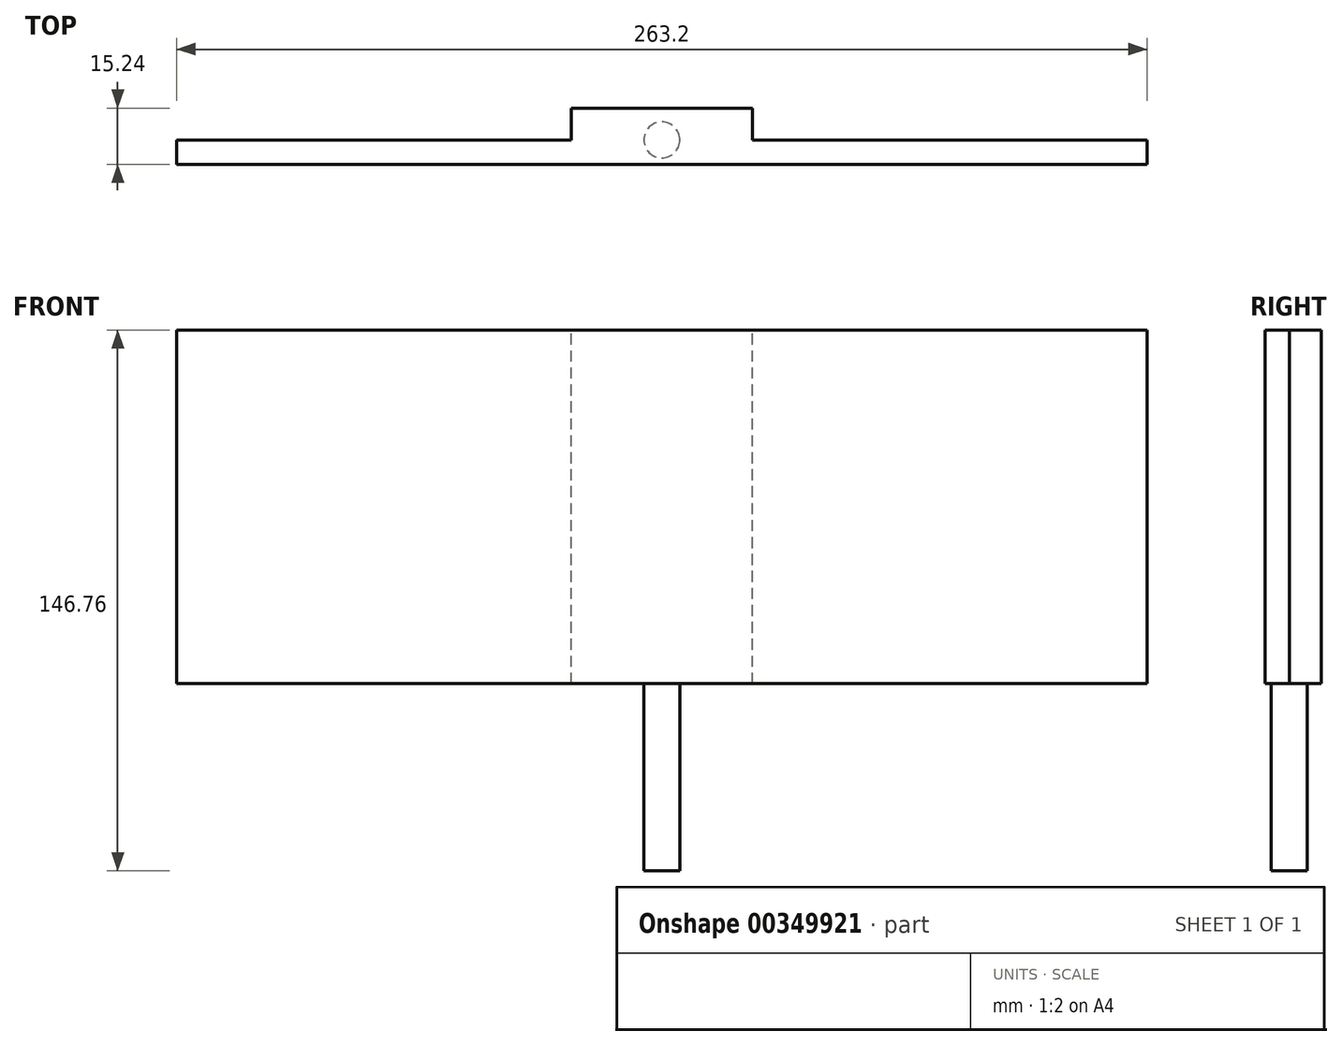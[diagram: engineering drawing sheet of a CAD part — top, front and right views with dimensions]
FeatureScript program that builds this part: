
annotation { "Feature Type Name" : "Feature", "Feature Type Description" : "" }
export const myFeature = defineFeature(function(context is Context, id is Id, definition is map)
    precondition{}
    {
        {
            var Q0;
            Q0=qCreatedBy(makeId("Front.planeOp"),FACE);
            var sketch = newSketch(context, id + "F0", { "sketchPlane" : qUnion([Q0])});
            skLineSegment(sketch, "E0.bottom", {"start": v(131.6, -47.98) * mm, "end": v(-131.6, -47.98) * mm});
            skLineSegment(sketch, "E0.top", {"start": v(131.6, 47.98) * mm, "end": v(-131.6, 47.98) * mm});
            skLineSegment(sketch, "E0.left", {"start": v(131.6, -47.98) * mm, "end": v(131.6, 47.98) * mm});
            skLineSegment(sketch, "E0.right", {"start": v(-131.6, -47.98) * mm, "end": v(-131.6, 47.98) * mm});
            skPoint(sketch, "E0.middle", {"position": v(0, 0) * mm});
            skSolve(sketch);
        }
        {
            var Q0;
            Q0 = qSketchRegion(id + "F0", true);
            extrude(context, id + "F1", {"entities" : qUnion([Q0]), "depth" : 6.6 * mm, "offsetDistance" : 25.4 * mm});
        }
        {
            var Q0;
            Q0=makeQuery(id+"F1.opExtrude","CAP_FACE",FACE,{"disambiguationData":[OSD([sQuery(id+"F0.wireOp",EDGE,"E0.bottom"),sQuery(id+"F0.wireOp",EDGE,"E0.top"),sQuery(id+"F0.wireOp",EDGE,"E0.left"),sQuery(id+"F0.wireOp",EDGE,"E0.right")])],"isStart":true});
            var sketch = newSketch(context, id + "F2", { "sketchPlane" : qUnion([Q0])});
            skLineSegment(sketch, "E1.bottom", {"start": v(24.51, -47.98) * mm, "end": v(-24.51, -47.98) * mm});
            skLineSegment(sketch, "E1.top", {"start": v(24.51, 47.98) * mm, "end": v(-24.51, 47.98) * mm});
            skLineSegment(sketch, "E1.left", {"start": v(24.51, -47.98) * mm, "end": v(24.51, 47.98) * mm});
            skLineSegment(sketch, "E1.right", {"start": v(-24.51, -47.98) * mm, "end": v(-24.51, 47.98) * mm});
            skPoint(sketch, "E1.middle", {"position": v(0, 0) * mm});
            skSolve(sketch);
        }
        {
            var Q0;
            Q0 = qSketchRegion(id + "F2", true);
            extrude(context, id + "F3", {"entities" : qUnion([Q0]), "operationType" : NewBodyOperationType.ADD, "depth" : 8.64 * mm, "offsetDistance" : 25.4 * mm});
        }
        {
            var Q0;
            Q0=makeQuery(id+"F3.boolean.opBoolean","MERGE",FACE,{"derivedFrom":[makeQuery(id+"F1.opExtrude","SWEPT_FACE",FACE,{"disambiguationData":[OSD([sQuery(id+"F0.wireOp",EDGE,"E0.bottom")])]}),makeQuery(id+"F3.opExtrude","SWEPT_FACE",FACE,{"disambiguationData":[OSD([sQuery(id+"F2.wireOp",EDGE,"E1.bottom")])]})]});
            var sketch = newSketch(context, id + "F4", { "sketchPlane" : qUnion([Q0])});
            skCircle(sketch, "E2", {"center": v(0, 0) * mm, "radius": 4.9 * mm});
            skSolve(sketch);
        }
        {
            var Q0;
            Q0 = qSketchRegion(id + "F4", true);
            extrude(context, id + "F5", {"entities" : qUnion([Q0]), "operationType" : NewBodyOperationType.ADD, "depth" : 50.8 * mm, "offsetDistance" : 25.4 * mm});
        }
    });
